# Revit family: QMX-HP_Horizontal_Level_1
name_source: partatom
category: Mechanical Equipment
units: mm (PartAtom-declared; Revit-internal decimal feet)

## family parameters
Always vertical = Yes
Cut with Voids When Loaded = No
OmniClass Number = 23.75.35.17
OmniClass Title = Fans
Part Type = Normal
Room Calculation Point = No
Round Connector Dimension = Use Radius
Shared = No
Work Plane-Based = No

## types (14) — shared parameters
0 = 0"
1.5 = 1 1/2"
1.9375 = 1 15/16"
3 = 3"
45 = 45.00°
90 = 90.00°
Manufacturer = Loren Cook Company
Model = QMX-HP Level 1
ONE EIGTH = 1/8"
ROTATION = 45.00°
Type Comments = Mixed Flow Inline Horizontal Mount Level 1 Belt Drive Arrangement 9
URL = www.lorencook.com

## per-type parameters (varying)
- 165-QMX-HP_HOR_LEVEL_1: (A/2)-.125=11 5/8"; (D/2)+1.5=16 9/16"; (J/2)-.75=11 1/2"; (M+3)/2=12 5/32"; (M/2)+2=12 21/32"; (M/2)-2=8 21/32"; -(B/2)=-16 1/2"; -(J/2)-.75=-11 1/2"; -B/3*2=-22"; -Feet_Height=-4"; A=23 1/2"; A/2=11 3/4"; A/4=5 7/8"; A/8=2 15/16"; B=33"; B/10=3 5/16"; B/2=16 1/2"; B/3*2=22"; B/6=5 1/2"; B/8=5 1/2"; C=26 1/2"; C/2=13 1/4"; D=30 1/8"; E=3/8"; E/2=3/16"; Feet_Height=4"; G=11 7/8"; G/2=12 1/4"; H=15 5/8"; J=24 1/2"; J+1.5=26"; J/2=12 1/4"; K=44 1/8"; K-D=29 13/16"; K-D-1.5=28 5/16"; L=14 5/16"; M=21 5/16"; M+1.5=22 13/16"; M-1.5=19 13/16"; M/2=10 21/32"; MCHALF=10"; MOTORCOVER=20"
- 180-QMX-HP_HOR_LEVEL_1: (A/2)-.125=12 11/16"; (D/2)+1.5=17 21/32"; (J/2)-.75=12 11/16"; (M+3)/2=12 15/16"; (M/2)+2=13 7/16"; (M/2)-2=9 7/16"; -(B/2)=-17 1/2"; -(J/2)-.75=-12 11/16"; -B/3*2=-23 11/32"; -Feet_Height=-5"; A=25 5/8"; A/2=12 13/16"; A/4=6 13/32"; A/8=3 7/32"; B=35"; B/10=3 1/2"; B/2=17 1/2"; B/3*2=23 11/32"; B/6=5 27/32"; B/8=5 27/32"; C=28 5/8"; C/2=14 5/16"; D=32 5/16"; E=3/8"; E/2=3/16"; Feet_Height=5"; G=9 3/8"; G/2=13 7/16"; H=19 3/8"; J=26 7/8"; J+1.5=28 3/8"; J/2=13 7/16"; K=46 7/8"; K-D=31 3/8"; K-D-1.5=29 7/8"; L=15 1/2"; M=22 7/8"; M+1.5=24 3/8"; M-1.5=21 3/8"; M/2=11 7/16"; MCHALF=10"; MOTORCOVER=20"
- 202-QMX-HP_HOR_LEVEL_1: (A/2)-.125=14 1/4"; (D/2)+1.5=19 1/4"; (J/2)-.75=13 11/16"; (M+3)/2=14 1/16"; (M/2)+2=14 9/16"; (M/2)-2=10 9/16"; -(B/2)=-18 3/4"; -(J/2)-.75=-13 11/16"; -B/3*2=-25"; -Feet_Height=-6"; A=28 3/4"; A/2=14 3/8"; A/4=7 3/16"; A/8=3 19/32"; B=37 1/2"; B/10=3 3/4"; B/2=18 3/4"; B/3*2=25"; B/6=6 1/4"; B/8=6 1/4"; C=31 3/4"; C/2=15 7/8"; D=35 1/2"; E=3/8"; E/2=3/16"; Feet_Height=6"; G=12"; G/2=14 7/16"; H=19 3/8"; J=28 7/8"; J+1.5=30 3/8"; J/2=14 7/16"; K=50 1/16"; K-D=32 13/16"; K-D-1.5=31 5/16"; L=17 1/4"; M=25 1/8"; M+1.5=26 5/8"; M-1.5=23 5/8"; M/2=12 9/16"; MCHALF=10"; MOTORCOVER=20"
- 225-QMX-HP_HOR_LEVEL_1: (A/2)-.125=15 27/32"; (D/2)+1.5=20 7/8"; (J/2)-.75=15 7/16"; (M+3)/2=15 3/16"; (M/2)+2=15 11/16"; (M/2)-2=11 11/16"; -(B/2)=-20 1/2"; -(J/2)-.75=-15 7/16"; -B/3*2=-27 11/32"; -Feet_Height=-7"; A=31 15/16"; A/2=15 31/32"; A/4=8"; A/8=4"; B=41"; B/10=4 3/32"; B/2=20 1/2"; B/3*2=27 11/32"; B/6=6 27/32"; B/8=6 27/32"; C=34 15/16"; C/2=17 15/32"; D=38 3/4"; E=3/8"; E/2=3/16"; Feet_Height=7"; G=15 1/2"; G/2=16 3/16"; H=19 3/8"; J=32 3/8"; J+1.5=33 7/8"; J/2=16 3/16"; K=53 11/16"; K-D=34 11/16"; K-D-1.5=33 3/16"; L=19"; M=27 3/8"; M+1.5=28 7/8"; M-1.5=25 7/8"; M/2=13 11/16"; MCHALF=10 21/32"; MOTORCOVER=21 9/32"
- 245-QMX-HP_HOR_LEVEL_1: (A/2)-.125=17 1/4"; (D/2)+1.5=22 9/32"; (J/2)-.75=17 3/16"; (M+3)/2=16 7/32"; (M/2)+2=16 23/32"; (M/2)-2=12 23/32"; -(B/2)=-22 1/4"; -(J/2)-.75=-17 3/16"; -B/3*2=-29 21/32"; -Feet_Height=-7 1/2"; A=34 3/4"; A/2=17 3/8"; A/4=8 11/16"; A/8=4 11/32"; B=44 1/2"; B/10=4 7/16"; B/2=22 1/4"; B/3*2=29 21/32"; B/6=7 13/32"; B/8=7 13/32"; C=37 3/4"; C/2=18 7/8"; D=41 9/16"; E=3/8"; E/2=3/16"; Feet_Height=7 1/2"; G=14 3/16"; G/2=17 15/16"; H=22 3/4"; J=35 7/8"; J+1.5=37 3/8"; J/2=17 15/16"; K=58 3/8"; K-D=37 7/8"; K-D-1.5=36 3/8"; L=20 1/2"; M=29 7/16"; M+1.5=30 15/16"; M-1.5=27 15/16"; M/2=14 23/32"; MCHALF=11 19/32"; MOTORCOVER=23 5/32"
- 270-QMX-HP_HOR_LEVEL_1: (A/2)-.125=19 1/32"; (D/2)+1.5=24 1/16"; (J/2)-.75=18 7/16"; (M+3)/2=17 15/32"; (M/2)+2=17 31/32"; (M/2)-2=13 31/32"; -(B/2)=-23 1/2"; -(J/2)-.75=-18 7/16"; -B/3*2=-31 11/32"; -Feet_Height=-8"; A=38 5/16"; A/2=19 5/32"; A/4=9 19/32"; A/8=4 25/32"; B=47"; B/10=4 11/16"; B/2=23 1/2"; B/3*2=31 11/32"; B/6=7 27/32"; B/8=7 27/32"; C=41 5/16"; C/2=20 21/32"; D=45 1/8"; E=3/8"; E/2=3/16"; Feet_Height=8"; G=14 3/16"; G/2=19 3/16"; H=26 3/8"; J=38 3/8"; J+1.5=39 7/8"; J/2=19 3/16"; K=63 7/8"; K-D=41 7/16"; K-D-1.5=39 15/16"; L=22 7/16"; M=31 15/16"; M+1.5=33 7/16"; M-1.5=30 7/16"; M/2=15 31/32"; MCHALF=12 25/32"; MOTORCOVER=25 17/32"
- 300-QMX-HP_HOR_LEVEL_1: (A/2)-.125=21 1/8"; (D/2)+1.5=26 3/16"; (J/2)-.75=21 15/16"; (M+3)/2=18 31/32"; (M/2)+2=19 15/32"; (M/2)-2=15 15/32"; -(B/2)=-27"; -(J/2)-.75=-21 15/16"; -B/3*2=-36"; -Feet_Height=-9"; A=42 1/2"; A/2=21 1/4"; A/4=10 5/8"; A/8=5 5/16"; B=54"; B/10=5 13/32"; B/2=27"; B/3*2=36"; B/6=9"; B/8=9"; C=45 1/2"; C/2=22 3/4"; D=49 3/8"; E=3/8"; E/2=3/16"; Feet_Height=9"; G=20 7/8"; G/2=22 11/16"; H=26 3/8"; J=45 3/8"; J+1.5=46 7/8"; J/2=22 11/16"; K=68 1/2"; K-D=43 3/4"; K-D-1.5=42 1/4"; L=24 3/4"; M=34 15/16"; M+1.5=36 7/16"; M-1.5=33 7/16"; M/2=17 15/32"; MCHALF=14 5/32"; MOTORCOVER=28 11/32"
- 330-QMX-HP_HOR_LEVEL_1: (A/2)-.125=23 1/4"; (D/2)+1.5=28 5/16"; (J/2)-.75=24 3/16"; (M+3)/2=20 15/32"; (M/2)+2=20 31/32"; (M/2)-2=16 31/32"; -(B/2)=-29 1/4"; -(J/2)-.75=-24 3/16"; -B/3*2=-39"; -Feet_Height=-9 1/2"; A=46 3/4"; A/2=23 3/8"; A/4=11 11/16"; A/8=5 27/32"; B=58 1/2"; B/10=5 27/32"; B/2=29 1/4"; B/3*2=39"; B/6=9 3/4"; B/8=9 3/4"; C=49 3/4"; C/2=24 7/8"; D=53 5/8"; E=3/8"; E/2=3/16"; Feet_Height=9 1/2"; G=25 9/16"; G/2=24 15/16"; H=26 3/8"; J=49 7/8"; J+1.5=51 3/8"; J/2=24 15/16"; K=72 9/16"; K-D=45 9/16"; K-D-1.5=44 1/16"; L=27"; M=37 15/16"; M+1.5=39 7/16"; M-1.5=36 7/16"; M/2=18 31/32"; MCHALF=15 19/32"; MOTORCOVER=31 5/32"
- 365-QMX-HP_HOR_LEVEL_1: (A/2)-.125=25 3/4"; (D/2)+1.5=31 1/4"; (J/2)-.75=26 15/16"; (M+3)/2=22 17/32"; (M/2)+2=23 1/32"; (M/2)-2=19 1/32"; -(B/2)=-32"; -(J/2)-.75=-26 15/16"; -B/3*2=-42 21/32"; -Feet_Height=-10"; A=51 3/4"; A/2=25 7/8"; A/4=12 15/16"; A/8=6 15/32"; B=64"; B/10=6 13/32"; B/2=32"; B/3*2=42 21/32"; B/6=10 21/32"; B/8=10 21/32"; C=54 3/4"; C/2=27 3/8"; D=59 1/2"; E=3/8"; E/2=3/16"; Feet_Height=10"; G=30 7/16"; G/2=27 11/16"; H=26 3/8"; J=55 3/8"; J+1.5=56 7/8"; J/2=27 11/16"; K=78 1/16"; K-D=48 1/4"; K-D-1.5=46 3/4"; L=29 13/16"; M=42 1/16"; M+1.5=43 9/16"; M-1.5=40 9/16"; M/2=21 1/32"; MCHALF=17 1/4"; MOTORCOVER=34 1/2"
- 402-QMX-HP_HOR_LEVEL_1: (A/2)-.125=28 11/32"; (D/2)+1.5=33 15/16"; (J/2)-.75=29 1/4"; (M+3)/2=24 13/32"; (M/2)+2=24 29/32"; (M/2)-2=20 29/32"; -(B/2)=-34 1/4"; -(J/2)-.75=-29 1/4"; -B/3*2=-45 21/32"; -Feet_Height=-11"; A=56 15/16"; A/2=28 15/32"; A/4=14 1/4"; A/8=7 1/8"; B=68 1/2"; B/10=6 27/32"; B/2=34 1/4"; B/3*2=45 21/32"; B/6=11 13/32"; B/8=11 13/32"; C=59 15/16"; C/2=29 31/32"; D=64 7/8"; E=3/8"; E/2=3/16"; Feet_Height=11"; G=32 15/16"; G/2=30"; H=26 3/8"; J=60"; J+1.5=61 1/2"; J/2=30"; K=85 7/8"; K-D=53 1/4"; K-D-1.5=51 3/4"; L=32 5/8"; M=45 13/16"; M+1.5=47 5/16"; M-1.5=44 5/16"; M/2=22 29/32"; MCHALF=18 31/32"; MOTORCOVER=37 31/32"
- 445-QMX-HP_HOR_LEVEL_1: (A/2)-.125=31 13/32"; (D/2)+1.5=36 15/16"; (J/2)-.75=32"; (M+3)/2=26 19/32"; (M/2)+2=27 3/32"; (M/2)-2=23 3/32"; -(B/2)=-37"; -(J/2)-.75=-32"; -B/3*2=-49 11/32"; -Feet_Height=-12"; A=63 1/16"; A/2=31 17/32"; A/4=15 25/32"; A/8=7 7/8"; B=74"; B/10=7 13/32"; B/2=37"; B/3*2=49 11/32"; B/6=12 11/32"; B/8=12 11/32"; C=66 1/16"; C/2=33 1/32"; D=70 7/8"; E=3/8"; E/2=3/16"; Feet_Height=12"; G=36 5/16"; G/2=32 3/4"; H=30 3/8"; J=65 1/2"; J+1.5=67"; J/2=32 3/4"; K=95 1/2"; K-D=59 7/8"; K-D-1.5=58 3/8"; L=35 5/8"; M=50 3/16"; M+1.5=51 11/16"; M-1.5=48 11/16"; M/2=25 3/32"; MCHALF=21 1/32"; MOTORCOVER=42 1/32"
- 490-QMX-HP_HOR_LEVEL_1: (A/2)-.125=34 9/16"; (D/2)+1.5=40 9/16"; (J/2)-.75=35 1/4"; (M+3)/2=29 1/8"; (M/2)+2=29 5/8"; (M/2)-2=25 5/8"; -(B/2)=-40 1/4"; -(J/2)-.75=-35 1/4"; -B/3*2=-53 21/32"; -Feet_Height=-12 1/2"; A=69 3/8"; A/2=34 11/16"; A/4=17 11/32"; A/8=8 11/16"; B=80 1/2"; B/10=8 1/16"; B/2=40 1/4"; B/3*2=53 21/32"; B/6=13 13/32"; B/8=13 13/32"; C=72 3/8"; C/2=36 3/16"; D=78 1/8"; E=3/8"; E/2=3/16"; Feet_Height=12 1/2"; G=42 7/8"; G/2=36"; H=30 3/8"; J=72"; J+1.5=73 1/2"; J/2=36"; K=101 5/8"; K-D=62 13/16"; K-D-1.5=61 5/16"; L=38 13/16"; M=55 1/4"; M+1.5=56 3/4"; M-1.5=53 3/4"; M/2=27 5/8"; MCHALF=23 1/8"; MOTORCOVER=46 1/4"
- 540-QMX-HP_HOR_LEVEL_1: (A/2)-.125=38 3/32"; (D/2)+1.5=44 3/32"; (J/2)-.75=38 1/2"; (M+3)/2=31 5/8"; (M/2)+2=32 1/8"; (M/2)-2=28 1/8"; -(B/2)=-43 1/2"; -(J/2)-.75=-38 1/2"; -B/3*2=-58"; -Feet_Height=-13"; A=76 7/16"; A/2=38 7/32"; A/4=19 1/8"; A/8=9 9/16"; B=87"; B/10=8 11/16"; B/2=43 1/2"; B/3*2=58"; B/6=14 1/2"; B/8=14 1/2"; C=79 9/16"; C/2=39 25/32"; D=85 3/16"; E=7/16"; E/2=7/32"; Feet_Height=13"; G=46 1/4"; G/2=39 1/4"; H=33 3/8"; J=78 1/2"; J+1.5=80"; J/2=39 1/4"; K=111"; K-D=68 5/8"; K-D-1.5=67 1/8"; L=42 3/8"; M=60 1/4"; M+1.5=61 3/4"; M-1.5=58 3/4"; M/2=30 1/8"; MCHALF=25 15/32"; MOTORCOVER=50 31/32"
- 600-QMX-HP_HOR_LEVEL_1: (A/2)-.125=42 5/16"; (D/2)+1.5=48 3/8"; (J/2)-.75=42 13/16"; (M+3)/2=34 21/32"; (M/2)+2=35 5/32"; (M/2)-2=31 5/32"; -(B/2)=-47 3/4"; -(J/2)-.75=-42 13/16"; -B/3*2=-63 21/32"; -Feet_Height=-14"; A=84 7/8"; A/2=42 7/16"; A/4=21 7/32"; A/8=10 5/8"; B=95 1/2"; B/10=9 9/16"; B/2=47 3/4"; B/3*2=63 21/32"; B/6=15 29/32"; B/8=15 29/32"; C=88"; C/2=44"; D=93 3/4"; E=7/16"; E/2=7/32"; Feet_Height=14"; G=54 11/16"; G/2=43 9/16"; H=33 3/8"; J=87 1/8"; J+1.5=88 5/8"; J/2=43 9/16"; K=119 11/16"; K-D=73 1/16"; K-D-1.5=71 9/16"; L=46 5/8"; M=66 5/16"; M+1.5=67 13/16"; M-1.5=64 13/16"; M/2=33 5/32"; MCHALF=25 15/32"; MOTORCOVER=50 31/32"

## geometry (parser evidence)
native form markers: Sweep x3
no freeform markers — native parametric forms only
